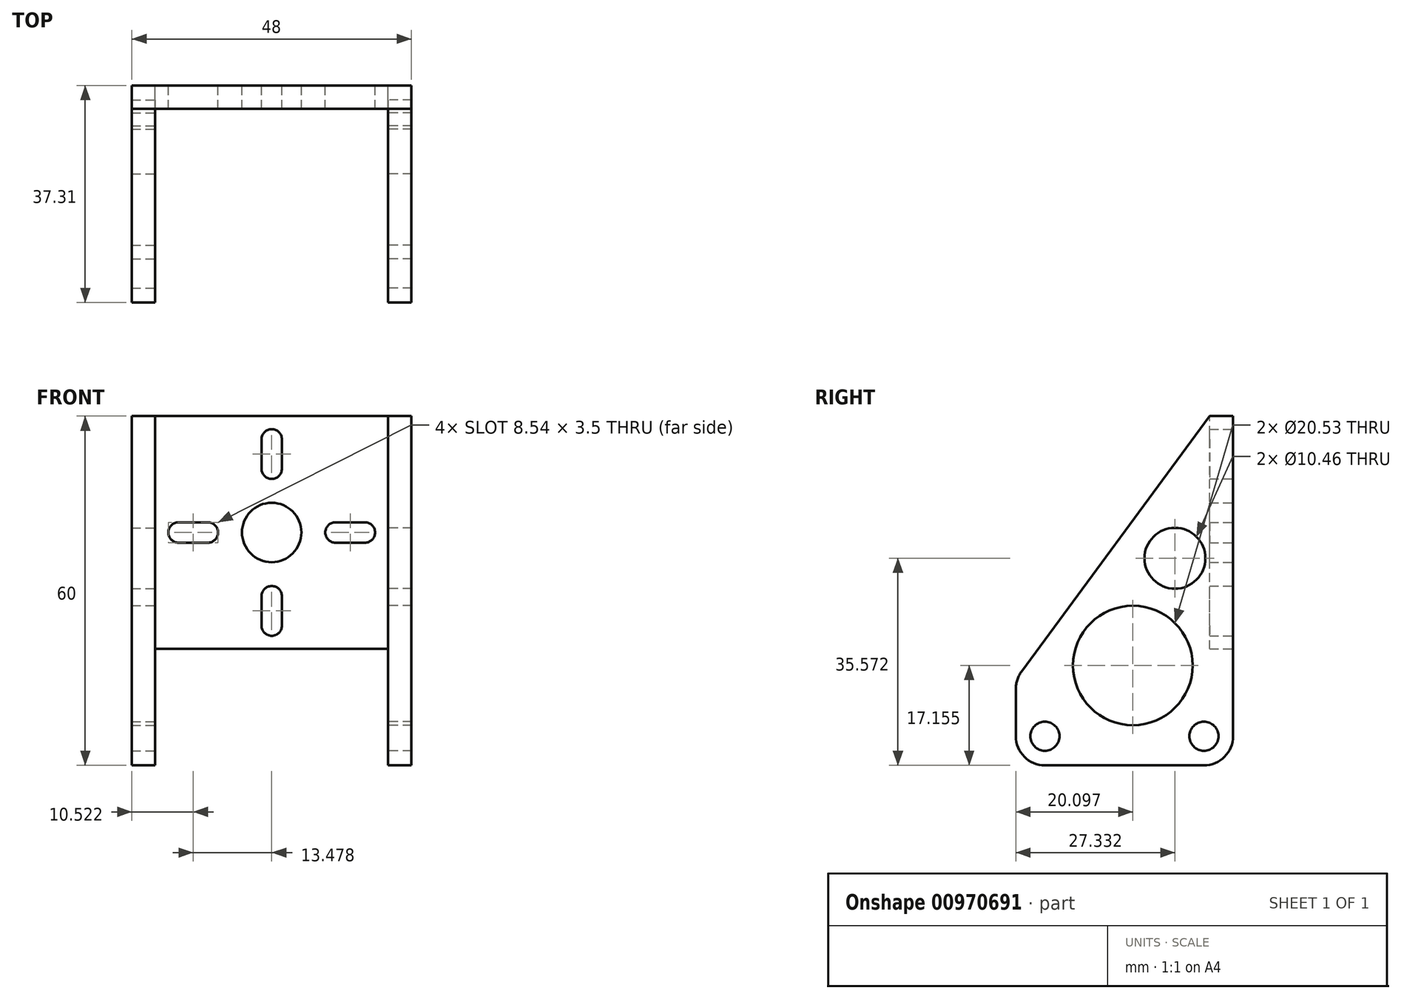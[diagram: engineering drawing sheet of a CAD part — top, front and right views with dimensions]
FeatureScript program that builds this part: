
annotation { "Feature Type Name" : "Feature", "Feature Type Description" : "" }
export const myFeature = defineFeature(function(context is Context, id is Id, definition is map)
    precondition{}
    {
        {
            var Q0;
            Q0=qCreatedBy(makeId("Front.planeOp"),FACE);
            var sketch = newSketch(context, id + "F0", { "sketchPlane" : qUnion([Q0])});
            skPoint(sketch, "E0", {"position": v(0, 40) * mm});
            skCircle(sketch, "E1", {"center": v(0, 40) * mm, "radius": 5.1 * mm});
            skLineSegment(sketch, "E2", {"start": v(-20, 60) * mm, "end": v(20, 60) * mm});
            skLineSegment(sketch, "E3", {"start": v(20, 60) * mm, "end": v(20, 20) * mm});
            skLineSegment(sketch, "E4", {"start": v(20, 20) * mm, "end": v(-20, 20) * mm});
            skLineSegment(sketch, "E5", {"start": v(-20, 20) * mm, "end": v(-20, 60) * mm});
            skLineSegment(sketch, "E6", {"start": v(0, 40) * mm, "end": v(-69.39, 40) * mm});
            skLineSegment(sketch, "E7", {"start": v(-69.39, 40) * mm, "end": v(68.28, 40) * mm});
            skLineSegment(sketch, "E8.bottom", {"start": v(-1.75, 50.96) * mm, "end": v(1.75, 50.96) * mm});
            skLineSegment(sketch, "E8.top", {"start": v(-1.75, 56) * mm, "end": v(1.75, 56) * mm});
            skLineSegment(sketch, "E8.left", {"start": v(-1.75, 56) * mm, "end": v(-1.75, 50.96) * mm});
            skLineSegment(sketch, "E8.right", {"start": v(1.75, 56) * mm, "end": v(1.75, 50.96) * mm});
            skCircle(sketch, "E9", {"center": v(0, 56) * mm, "radius": 1.75 * mm});
            skCircle(sketch, "E10", {"center": v(0, 50.96) * mm, "radius": 1.75 * mm});
            skCircle(sketch, "E11.1.0", {"center": v(-16, 40) * mm, "radius": 1.75 * mm});
            skLineSegment(sketch, "E11.1.1", {"start": v(-16, 38.25) * mm, "end": v(-10.96, 38.25) * mm});
            skLineSegment(sketch, "E11.1.2", {"start": v(-16, 38.25) * mm, "end": v(-16, 41.75) * mm});
            skLineSegment(sketch, "E11.1.3", {"start": v(-16, 41.75) * mm, "end": v(-10.96, 41.75) * mm});
            skLineSegment(sketch, "E11.1.4", {"start": v(-10.96, 38.25) * mm, "end": v(-10.96, 41.75) * mm});
            skCircle(sketch, "E11.1.5", {"center": v(-10.96, 40) * mm, "radius": 1.75 * mm});
            skCircle(sketch, "E11.2.0", {"center": v(0, 24) * mm, "radius": 1.75 * mm});
            skLineSegment(sketch, "E11.2.1", {"start": v(1.75, 24) * mm, "end": v(1.75, 29.04) * mm});
            skLineSegment(sketch, "E11.2.2", {"start": v(1.75, 24) * mm, "end": v(-1.75, 24) * mm});
            skLineSegment(sketch, "E11.2.3", {"start": v(-1.75, 24) * mm, "end": v(-1.75, 29.04) * mm});
            skLineSegment(sketch, "E11.2.4", {"start": v(1.75, 29.04) * mm, "end": v(-1.75, 29.04) * mm});
            skCircle(sketch, "E11.2.5", {"center": v(0, 29.04) * mm, "radius": 1.75 * mm});
            skCircle(sketch, "E11.3.0", {"center": v(16, 40) * mm, "radius": 1.75 * mm});
            skLineSegment(sketch, "E11.3.1", {"start": v(16, 41.75) * mm, "end": v(10.96, 41.75) * mm});
            skLineSegment(sketch, "E11.3.2", {"start": v(16, 41.75) * mm, "end": v(16, 38.25) * mm});
            skLineSegment(sketch, "E11.3.3", {"start": v(16, 38.25) * mm, "end": v(10.96, 38.25) * mm});
            skLineSegment(sketch, "E11.3.4", {"start": v(10.96, 41.75) * mm, "end": v(10.96, 38.25) * mm});
            skCircle(sketch, "E11.3.5", {"center": v(10.96, 40) * mm, "radius": 1.75 * mm});
            skLineSegment(sketch, "E11.anchor1", {"start": v(0, 40) * mm, "end": v(0, 50.96) * mm, "construction": true});
            skLineSegment(sketch, "E11.anchor2", {"start": v(0, 40) * mm, "end": v(10.96, 40) * mm, "construction": true});
            skSolve(sketch);
        }
        {
            var Q0;
            Q0 = qSketchRegion(id + "F0", true);
            extrude(context, id + "F1", {"entities" : qUnion([Q0]), "depth" : 4 * mm, "offsetDistance" : 25 * mm});
        }
        {
            var Q0;
            Q0=makeQuery(id+"F1.opExtrude","SWEPT_FACE",FACE,{"disambiguationData":[OSD([sQuery(id+"F0.wireOp",EDGE,"E3")])]});
            var sketch = newSketch(context, id + "F2", { "sketchPlane" : qUnion([Q0])});
            skLineSegment(sketch, "E12", {"start": v(-5, 0) * mm, "end": v(-32.3, 0) * mm});
            skLineSegment(sketch, "E13", {"start": v(-37.3, 5) * mm, "end": v(-37.3, 13.12) * mm});
            skLineSegment(sketch, "E14", {"start": v(-36.33, 16.08) * mm, "end": v(-4, 60) * mm});
            skLineSegment(sketch, "E15", {"start": v(-4, 60) * mm, "end": v(0, 60) * mm});
            skLineSegment(sketch, "E16", {"start": v(0, 60) * mm, "end": v(0, 5) * mm});
            skPoint(sketch, "E17.visualSharp", {"position": v(-37.3, 14.76) * mm});
            skArc(sketch, "E17.filletArc", {"start": v(-36.33, 16.08) * mm, "mid": v(-37.06, 14.68) * mm, "end": v(-37.3, 13.12) * mm});
            skPoint(sketch, "E18.visualSharp", {"position": v(-37.3, 0) * mm});
            skArc(sketch, "E18.filletArc", {"start": v(-37.3, 5) * mm, "mid": v(-35.84, 1.46) * mm, "end": v(-32.3, 0) * mm});
            skPoint(sketch, "E19.visualSharp", {"position": v(0, 0) * mm});
            skArc(sketch, "E19.filletArc", {"start": v(-5, 0) * mm, "mid": v(-1.46, 1.46) * mm, "end": v(0, 5) * mm});
            skCircle(sketch, "E20", {"center": v(-5, 5) * mm, "radius": 2.5 * mm});
            skCircle(sketch, "E21", {"center": v(-32.3, 5) * mm, "radius": 2.5 * mm});
            skCircle(sketch, "E22", {"center": v(-17.21, 17.15) * mm, "radius": 10.27 * mm});
            skCircle(sketch, "E23", {"center": v(-9.98, 35.57) * mm, "radius": 5.23 * mm});
            skSolve(sketch);
        }
        {
            var Q0;
            Q0 = qSketchRegion(id + "F2", true);
            extrude(context, id + "F3", {"entities" : qUnion([Q0]), "operationType" : NewBodyOperationType.ADD, "depth" : 4 * mm, "offsetDistance" : 25 * mm});
        }
        {
            var Q0;
            Q0=makeQuery(id+"F1.opExtrude","CAP_VERTEX",VERTEX,{"disambiguationData":[OSD([sQuery(id+"F0.wireOp",EDGE,"E2"),sQuery(id+"F0.wireOp",EDGE,"E5")])],"isStart":false});
            var Q1;
            Q1=makeQuery(id+"F1.opExtrude","CAP_VERTEX",VERTEX,{"disambiguationData":[OSD([sQuery(id+"F0.wireOp",EDGE,"E2"),sQuery(id+"F0.wireOp",EDGE,"E5")])],"isStart":true});
            var Q2;
            Q2=makeQuery(id+"F1.opExtrude","CAP_VERTEX",VERTEX,{"disambiguationData":[OSD([sQuery(id+"F0.wireOp",EDGE,"E4"),sQuery(id+"F0.wireOp",EDGE,"E5")])],"isStart":true});
            cPlane(context, id + "F4", {"entities" : qUnion([Q0, Q1, Q2]), "cplaneType" : CPlaneType.THREE_POINT, "offset" : 25 * mm, "width" : 150 * mm, "height" : 150 * mm});
        }
        {
            var Q0;
            Q0=qCreatedBy(id+"F4.planeOp",FACE);
            var sketch = newSketch(context, id + "F5", { "sketchPlane" : qUnion([Q0])});
            skLineSegment(sketch, "E24", {"start": v(-5, 0) * mm, "end": v(-32.3, 0) * mm});
            skLineSegment(sketch, "E25", {"start": v(-37.3, 5) * mm, "end": v(-37.3, 13.12) * mm});
            skLineSegment(sketch, "E26", {"start": v(-24.02, 32.8) * mm, "end": v(-4, 60) * mm});
            skLineSegment(sketch, "E27", {"start": v(-4, 60) * mm, "end": v(0, 60) * mm});
            skLineSegment(sketch, "E28", {"start": v(0, 60) * mm, "end": v(0, 5) * mm});
            skPoint(sketch, "E29.visualSharp", {"position": v(-37.3, 14.76) * mm});
            skArc(sketch, "E29.filletArc", {"start": v(-36.33, 16.08) * mm, "mid": v(-37.06, 14.68) * mm, "end": v(-37.3, 13.12) * mm});
            skPoint(sketch, "E30.visualSharp", {"position": v(-37.3, 0) * mm});
            skArc(sketch, "E30.filletArc", {"start": v(-37.3, 5) * mm, "mid": v(-35.84, 1.46) * mm, "end": v(-32.3, 0) * mm});
            skPoint(sketch, "E31.visualSharp", {"position": v(0, 0) * mm});
            skArc(sketch, "E31.filletArc", {"start": v(-5, 0) * mm, "mid": v(-1.46, 1.46) * mm, "end": v(0, 5) * mm});
            skCircle(sketch, "E32", {"center": v(-5, 5) * mm, "radius": 2.5 * mm});
            skCircle(sketch, "E33", {"center": v(-32.3, 5) * mm, "radius": 2.5 * mm});
            skCircle(sketch, "E34", {"center": v(-17.21, 17.15) * mm, "radius": 10.27 * mm});
            skCircle(sketch, "E35", {"center": v(-9.98, 35.57) * mm, "radius": 5.23 * mm});
            skLineSegment(sketch, "E36", {"start": v(-24.02, 32.8) * mm, "end": v(-36.33, 16.08) * mm});
            skSolve(sketch);
        }
        {
            var Q0;
            Q0=makeQuery(id+"F5.imprint","IMPRINT",FACE,{"disambiguationData":[TD([[makeQuery(id+"F5.imprint","IMPRINT",EDGE,{"derivedFrom":sQuery(id+"F5.wireOp",EDGE,"E24")}),-1.0]])]});
            extrude(context, id + "F6", {"entities" : qUnion([Q0]), "operationType" : NewBodyOperationType.ADD, "oppositeDirection" : true, "depth" : 4 * mm, "offsetDistance" : 25 * mm});
        }
    });
